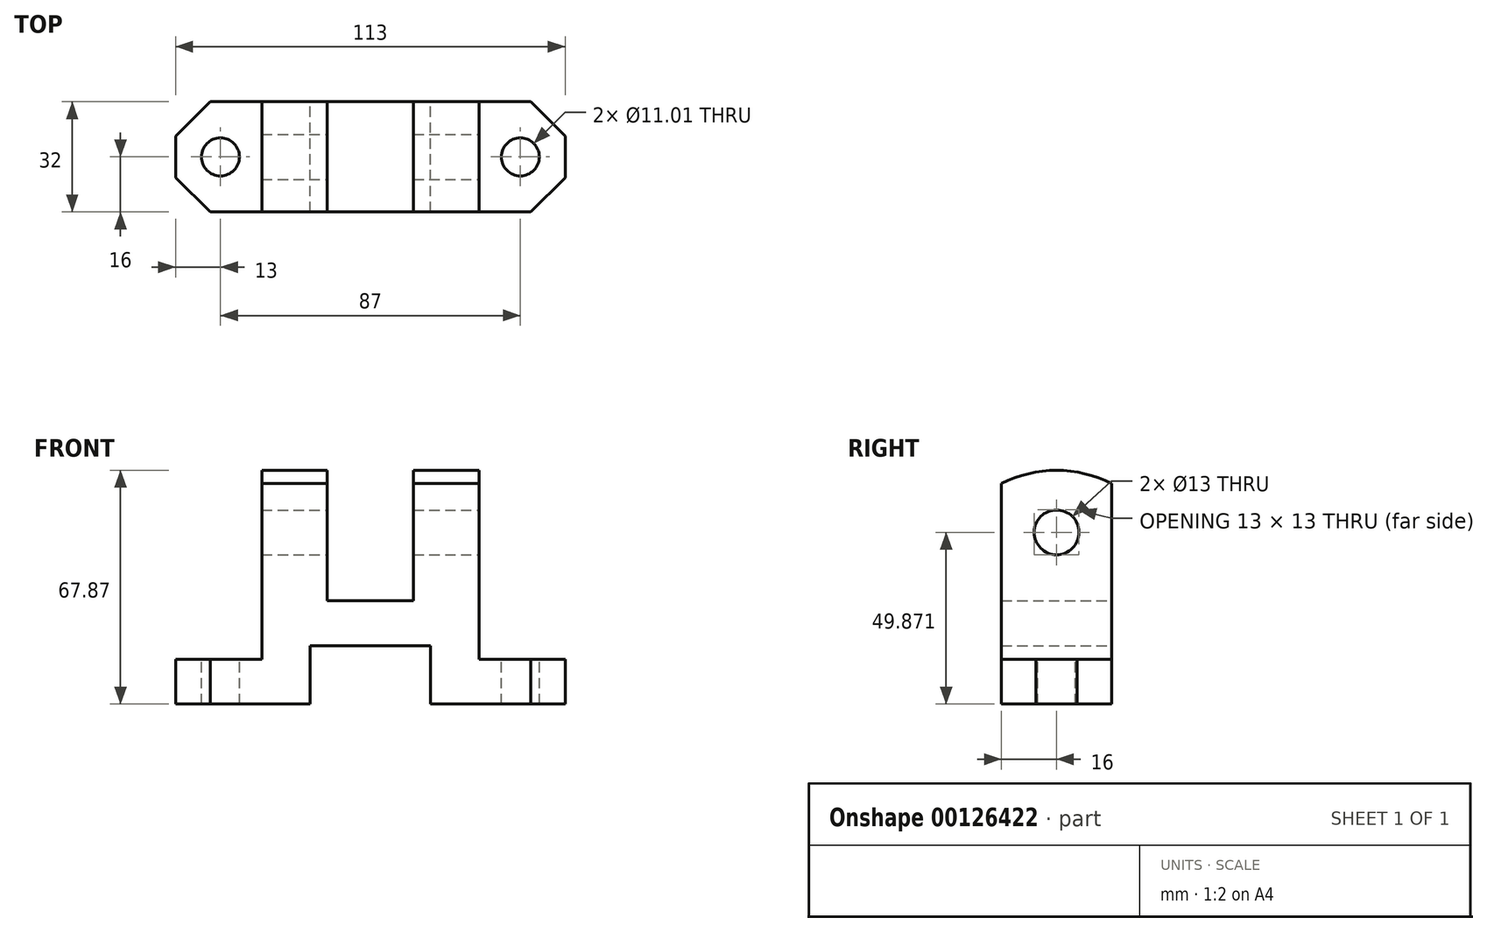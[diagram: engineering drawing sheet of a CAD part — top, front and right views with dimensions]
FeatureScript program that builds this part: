
annotation { "Feature Type Name" : "Feature", "Feature Type Description" : "" }
export const myFeature = defineFeature(function(context is Context, id is Id, definition is map)
    precondition{}
    {
        {
            var Q0;
            Q0=qCreatedBy(makeId("Front.planeOp"),FACE);
            var sketch = newSketch(context, id + "F0", { "sketchPlane" : qUnion([Q0])});
            skLineSegment(sketch, "E0", {"start": v(-25, 0) * mm, "end": v(-25, 13) * mm});
            skLineSegment(sketch, "E1", {"start": v(-25, 13) * mm, "end": v(0, 13) * mm});
            skLineSegment(sketch, "E2", {"start": v(0, 13) * mm, "end": v(0, 64) * mm});
            skLineSegment(sketch, "E3", {"start": v(0, 64) * mm, "end": v(19, 64) * mm});
            skLineSegment(sketch, "E4", {"start": v(19, 64) * mm, "end": v(19, 30) * mm});
            skLineSegment(sketch, "E5", {"start": v(19, 30) * mm, "end": v(44, 30) * mm});
            skLineSegment(sketch, "E6", {"start": v(44, 30) * mm, "end": v(44, 64) * mm});
            skLineSegment(sketch, "E7", {"start": v(44, 64) * mm, "end": v(63, 64) * mm});
            skLineSegment(sketch, "E8", {"start": v(63, 64) * mm, "end": v(63, 13) * mm});
            skLineSegment(sketch, "E9", {"start": v(63, 13) * mm, "end": v(88, 13) * mm});
            skLineSegment(sketch, "E10", {"start": v(88, 13) * mm, "end": v(88, 0) * mm});
            skLineSegment(sketch, "E11", {"start": v(49, 0) * mm, "end": v(49, 17) * mm});
            skLineSegment(sketch, "E12", {"start": v(49, 17) * mm, "end": v(14, 17) * mm});
            skLineSegment(sketch, "E13", {"start": v(14, 17) * mm, "end": v(14, 0) * mm});
            skLineSegment(sketch, "E14", {"start": v(14, 0) * mm, "end": v(49, 0) * mm});
            skLineSegment(sketch, "E15", {"start": v(-25, 0) * mm, "end": v(14, 0) * mm});
            skLineSegment(sketch, "E16", {"start": v(49, 0) * mm, "end": v(88, 0) * mm});
            skSolve(sketch);
        }
        {
            var Q0;
            Q0=makeQuery(id+"F0.imprint","IMPRINT",FACE,{"disambiguationData":[TD([[makeQuery(id+"F0.imprint","IMPRINT",EDGE,{"derivedFrom":sQuery(id+"F0.wireOp",EDGE,"E0")}),-1.0]])]});
            extrude(context, id + "F1", {"entities" : qUnion([Q0]), "depth" : 32 * mm});
        }
        {
            var Q0;
            Q0=makeQuery(id+"F1.opExtrude","SWEPT_FACE",FACE,{"disambiguationData":[OSD([sQuery(id+"F0.wireOp",EDGE,"E8")])]});
            var sketch = newSketch(context, id + "F2", { "sketchPlane" : qUnion([Q0])});
            skArc(sketch, "E17", {"start": v(0, 64) * mm, "mid": v(-16, 67.87) * mm, "end": v(-32, 64) * mm});
            skLineSegment(sketch, "E18", {"start": v(-32, 64) * mm, "end": v(0, 64) * mm});
            skSolve(sketch);
        }
        {
            var Q0;
            Q0=makeQuery(id+"F2.imprint","IMPRINT",FACE,{"disambiguationData":[TD([[makeQuery(id+"F2.imprint","IMPRINT",EDGE,{"derivedFrom":sQuery(id+"F2.wireOp",EDGE,"E17")}),1.0]])]});
            extrude(context, id + "F3", {"entities" : qUnion([Q0]), "operationType" : NewBodyOperationType.ADD, "oppositeDirection" : true, "depth" : 19 * mm});
        }
        {
            var Q0;
            Q0=makeQuery(id+"F1.opExtrude","SWEPT_FACE",FACE,{"disambiguationData":[OSD([sQuery(id+"F0.wireOp",EDGE,"E2")])]});
            var sketch = newSketch(context, id + "F4", { "sketchPlane" : qUnion([Q0])});
            skArc(sketch, "E19", {"start": v(32, 64) * mm, "mid": v(16, 67.87) * mm, "end": v(0, 64) * mm});
            skLineSegment(sketch, "E20", {"start": v(0, 64) * mm, "end": v(32, 64) * mm});
            skSolve(sketch);
        }
        {
            var Q0;
            Q0=makeQuery(id+"F4.imprint","IMPRINT",FACE,{"disambiguationData":[TD([[makeQuery(id+"F4.imprint","IMPRINT",EDGE,{"derivedFrom":sQuery(id+"F4.wireOp",EDGE,"E19")}),1.0]])]});
            extrude(context, id + "F5", {"entities" : qUnion([Q0]), "operationType" : NewBodyOperationType.ADD, "oppositeDirection" : true, "depth" : 19 * mm});
        }
        {
            var Q0;
            Q0=makeQuery(id+"F1.opExtrude","SWEPT_FACE",FACE,{"disambiguationData":[OSD([sQuery(id+"F0.wireOp",EDGE,"E1")])]});
            var sketch = newSketch(context, id + "F6", { "sketchPlane" : qUnion([Q0])});
            skLineSegment(sketch, "E21", {"start": v(-15, 0) * mm, "end": v(-25, 0) * mm});
            skLineSegment(sketch, "E22", {"start": v(-25, 0) * mm, "end": v(-25, -10) * mm});
            skLineSegment(sketch, "E23", {"start": v(-25, -10) * mm, "end": v(-15, 0) * mm});
            skLineSegment(sketch, "E24", {"start": v(-25, -32) * mm, "end": v(-15, -32) * mm});
            skLineSegment(sketch, "E25", {"start": v(-15, -32) * mm, "end": v(-25, -22) * mm});
            skLineSegment(sketch, "E26", {"start": v(-25, -22) * mm, "end": v(-25, -32) * mm});
            skSolve(sketch);
        }
        {
            var Q0;
            Q0 = qSketchRegion(id + "F6", true);
            extrude(context, id + "F7", {"entities" : qUnion([Q0]), "operationType" : NewBodyOperationType.REMOVE, "oppositeDirection" : true, "depth" : 25 * mm});
        }
        {
            var Q0;
            Q0=makeQuery(id+"F1.opExtrude","SWEPT_FACE",FACE,{"disambiguationData":[OSD([sQuery(id+"F0.wireOp",EDGE,"E9")])]});
            var sketch = newSketch(context, id + "F8", { "sketchPlane" : qUnion([Q0])});
            skLineSegment(sketch, "E27", {"start": v(78, 0) * mm, "end": v(88, -10) * mm});
            skLineSegment(sketch, "E28", {"start": v(88, -10) * mm, "end": v(88, 0) * mm});
            skLineSegment(sketch, "E29", {"start": v(78, 0) * mm, "end": v(88, 0) * mm});
            skLineSegment(sketch, "E30", {"start": v(88, -32) * mm, "end": v(88, -22) * mm});
            skLineSegment(sketch, "E31", {"start": v(88, -22) * mm, "end": v(78, -32) * mm});
            skLineSegment(sketch, "E32", {"start": v(78, -32) * mm, "end": v(88, -32) * mm});
            skLineSegment(sketch, "E33", {"start": v(88, 0) * mm, "end": v(88, -16) * mm, "construction": true});
            skLineSegment(sketch, "E34", {"start": v(88, -16) * mm, "end": v(-28, -16) * mm, "construction": true});
            skPoint(sketch, "E34.endSnap0", {"position": v(63, -16) * mm});
            skCircle(sketch, "E35", {"center": v(75, -16) * mm, "radius": 5.5 * mm});
            skCircle(sketch, "E36", {"center": v(-12, -16) * mm, "radius": 5.5 * mm});
            skSolve(sketch);
        }
        {
            var Q0;
            Q0=makeQuery(id+"F8.imprint","IMPRINT",FACE,{"disambiguationData":[TD([[makeQuery(id+"F8.imprint","IMPRINT",EDGE,{"derivedFrom":sQuery(id+"F8.wireOp",EDGE,"E35")}),1.0]])]});
            var Q1;
            Q1=makeQuery(id+"F8.imprint","IMPRINT",FACE,{"disambiguationData":[TD([[makeQuery(id+"F8.imprint","IMPRINT",EDGE,{"derivedFrom":sQuery(id+"F8.wireOp",EDGE,"E27")}),1.0]])]});
            var Q2;
            Q2=makeQuery(id+"F8.imprint","IMPRINT",FACE,{"disambiguationData":[TD([[makeQuery(id+"F8.imprint","IMPRINT",EDGE,{"derivedFrom":sQuery(id+"F8.wireOp",EDGE,"E30")}),1.0]])]});
            var Q3;
            Q3=makeQuery(id+"F8.imprint","IMPRINT",FACE,{"disambiguationData":[TD([[makeQuery(id+"F8.imprint","IMPRINT",EDGE,{"derivedFrom":sQuery(id+"F8.wireOp",EDGE,"E36")}),1.0]])]});
            extrude(context, id + "F9", {"entities" : qUnion([Q0, Q1, Q2, Q3]), "operationType" : NewBodyOperationType.REMOVE, "endBound" : BoundingType.THROUGH_ALL, "oppositeDirection" : true, "depth" : 25 * mm});
        }
        {
            var Q0;
            Q0=makeQuery(id+"F3.boolean.opBoolean","MERGE",FACE,{"derivedFrom":[makeQuery(id+"F1.opExtrude","SWEPT_FACE",FACE,{"disambiguationData":[OSD([sQuery(id+"F0.wireOp",EDGE,"E8")])]}),makeQuery(id+"F3.opExtrude","CAP_FACE",FACE,{"disambiguationData":[OSD([sQuery(id+"F2.wireOp",EDGE,"E17"),sQuery(id+"F2.wireOp",EDGE,"E18")])],"isStart":true})]});
            var sketch = newSketch(context, id + "F10", { "sketchPlane" : qUnion([Q0])});
            skLineSegment(sketch, "E37", {"start": v(-32, 64) * mm, "end": v(0, 64) * mm, "construction": true});
            skLineSegment(sketch, "E38", {"start": v(0, 64) * mm, "end": v(-16, 64) * mm, "construction": true});
            skLineSegment(sketch, "E39", {"start": v(-16, 64) * mm, "end": v(-16, 67.87) * mm, "construction": true});
            skLineSegment(sketch, "E40", {"start": v(-16, 67.87) * mm, "end": v(-16, 64) * mm, "construction": true});
            skLineSegment(sketch, "E41", {"start": v(-16, 64) * mm, "end": v(-16, 13) * mm, "construction": true});
            skLineSegment(sketch, "E42", {"start": v(-16, 13) * mm, "end": v(-16, 49.87) * mm, "construction": true});
            skCircle(sketch, "E43", {"center": v(-16, 49.87) * mm, "radius": 6.5 * mm});
            skSolve(sketch);
        }
        {
            var Q0;
            Q0=makeQuery(id+"F10.imprint","IMPRINT",FACE,{"disambiguationData":[TD([[makeQuery(id+"F10.imprint","IMPRINT",EDGE,{"derivedFrom":sQuery(id+"F10.wireOp",EDGE,"E43")}),1.0]])]});
            extrude(context, id + "F11", {"entities" : qUnion([Q0]), "operationType" : NewBodyOperationType.REMOVE, "endBound" : BoundingType.THROUGH_ALL, "oppositeDirection" : true, "depth" : 25 * mm});
        }
    });
